# Revit family: Window_Shade-Draper_Inc.-Clutch_Flexshade
name_source: partatom
category: Specialty Equipment
revit_build: Autodesk Revit Architecture 2012 (Build: 20110309_2315(x64)
units: mm (PartAtom-declared; Revit-internal decimal feet)

## types (8) — shared parameters
C2 = 3/4"
Case Material = Paint - Draper - White
D1 = 5/8"
Description = Bead Chain Clutch Window Shade
Manufacturer = Draper Inc.
Model = Bead Chain Clutch Operating System
Notes = Maximum size 144” x 144”. Other sizes available. Contact Draper for details.
Product Documentation Link = http://www.draperinc.com
Product Name = Bead Chain Clutch Operating System
Product Page URL = http://www.draperinc.com
Shade Material = Fabric - Draper - Green Screen Revive 5%
URL = http://www.DraperInc.com

## per-type parameters (varying)
| type | A1 | A2 | B1 | B2 | Brackets Only | C Length | C1 | Depth | E1 | Head Box | Length | Not BO | Overall Height | Radius Fascia | Square Fascia | Width |
| Square Fascia - Large | 4 11/16" | 3 1/4" | 4 11/16" | 2 1/4" | No | 8' - 2 7/8" | 1 9/16" | 4 11/16" | 3/32" | No | 8' - 2 7/8" | Yes | 5' - 9 1/2" | No | Yes | 4 11/16" |
| Square Fascia - Small | 3 15/16" | 2 1/2" | 3 7/16" | 1 5/8" | No | 4' - 0" | 1 3/16" | 3 15/16" | 1/16" | No | 4' - 0" | Yes | 6' - 0" | No | Yes | 3 7/16" |
| Radius Fascia - Large | 4 11/16" | 3 1/4" | 4 11/16" | 2 1/4" | No | 8' - 2 7/8" | 1 9/16" | 4 11/16" | 3/32" | No | 8' - 2 7/8" | Yes | 5' - 9 1/2" | Yes | No | 4 11/16" |
| Radius Fascia - Small | 3 15/16" | 2 1/2" | 3 7/16" | 1 5/8" | No | 4' - 0" | 1 3/16" | 3 15/16" | 1/16" | No | 4' - 0" | Yes | 6' - 0" | Yes | No | 3 7/16" |
| Headbox - Small | 3 15/16" | 2 1/2" | 3 7/16" | 1 5/8" | No | 4' - 0" | 1 3/16" | 3 15/16" | 1/16" | Yes | 4' - 0" | Yes | 6' - 0" | No | No | 3 7/16" |
| Headbox - Large | 4 11/16" | 3 1/4" | 4 11/16" | 2 1/4" | No | 8' - 2 7/8" | 1 9/16" | 4 11/16" | 3/32" | Yes | 8' - 2 7/8" | Yes | 5' - 9 1/2" | No | No | 4 11/16" |
| Brackets Only - Large | 4 11/16" | 3 1/4" | 4 11/16" | 2 1/4" | Yes | 8' - 2 7/8" | 1 9/16" | 4 11/16" | 3/32" | No | 8' - 2 7/8" | No | 5' - 9 1/2" | No | No | 4 11/16" |
| Brackets Only - Small | 3 15/16" | 2 1/2" | 3 7/16" | 1 5/8" | Yes | 4' - 0" | 1 3/16" | 3 15/16" | 1/16" | No | 4' - 0" | No | 6' - 0" | No | No | 3 7/16" |

## geometry (parser evidence)
native form markers: Blend x1, Sweep x11
no freeform markers — native parametric forms only
